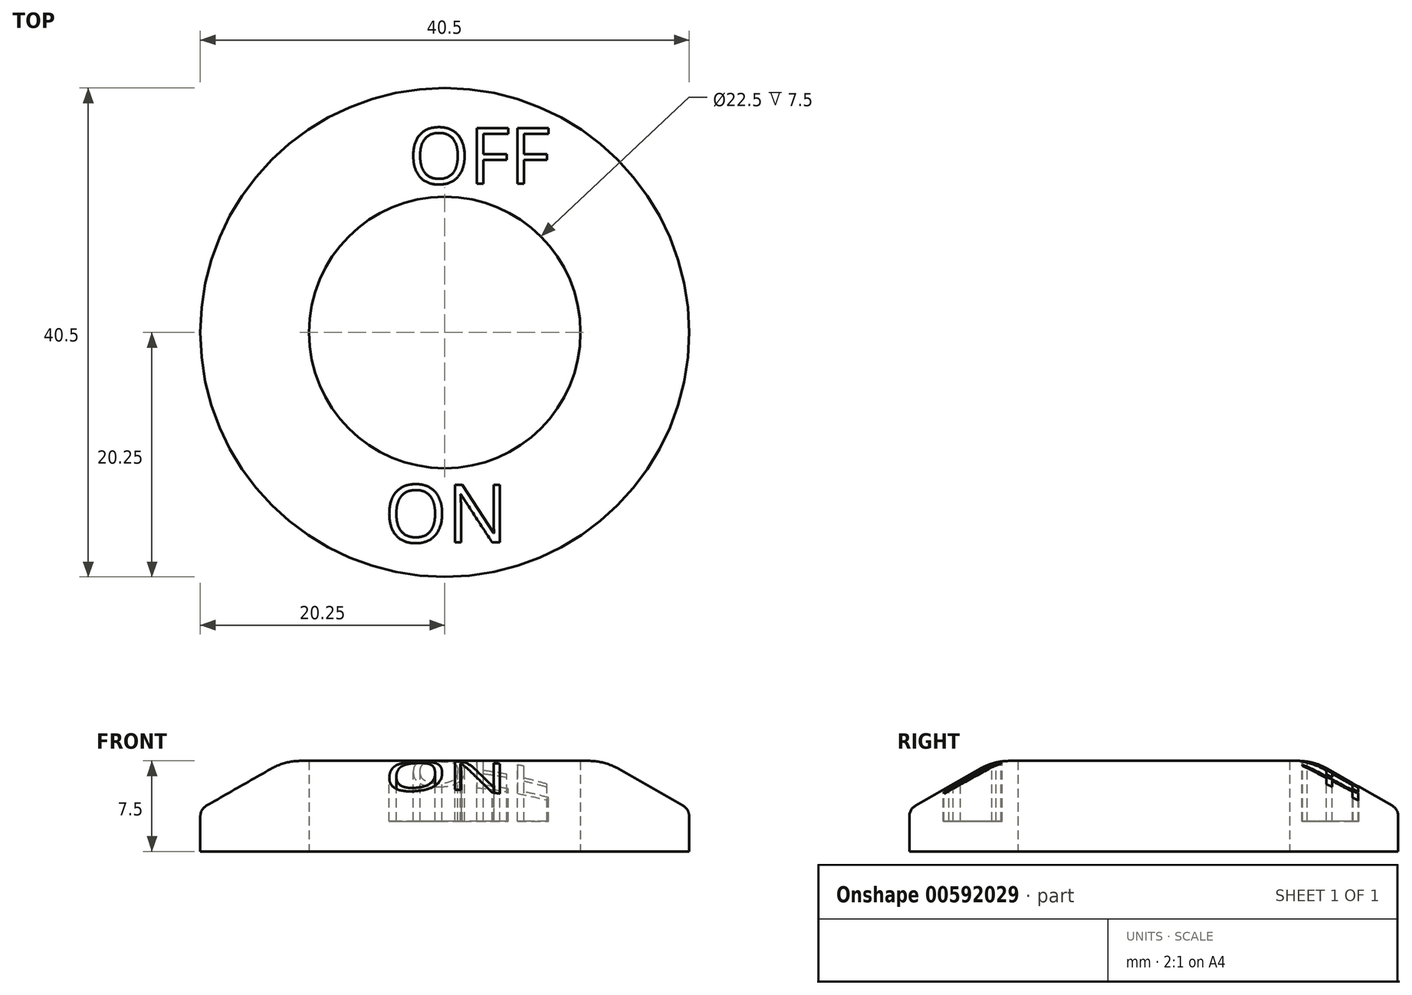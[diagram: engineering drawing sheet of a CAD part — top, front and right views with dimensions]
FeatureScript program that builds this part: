
annotation { "Feature Type Name" : "Feature", "Feature Type Description" : "" }
export const myFeature = defineFeature(function(context is Context, id is Id, definition is map)
    precondition{}
    {
        {
            var Q0;
            Q0=qCreatedBy(makeId("Top.planeOp"),FACE);
            var sketch = newSketch(context, id + "F0", { "sketchPlane" : qUnion([Q0])});
            skCircle(sketch, "E0", {"center": v(0, 0) * mm, "radius": 20.25 * mm});
            skSolve(sketch);
        }
        {
            var Q0;
            Q0=qCreatedBy(makeId("Top.planeOp"),FACE);
            cPlane(context, id + "F1", {"entities" : qUnion([Q0]), "cplaneType" : CPlaneType.OFFSET, "offset" : 7.5 * mm, "width" : 150 * mm, "height" : 150 * mm});
        }
        {
            var Q0;
            Q0=qCreatedBy(id+"F1.planeOp",FACE);
            var sketch = newSketch(context, id + "F2", { "sketchPlane" : qUnion([Q0])});
            skCircle(sketch, "E1", {"center": v(0, 0) * mm, "radius": 13.25 * mm});
            skSolve(sketch);
        }
        {
            var Q0;
            Q0=makeQuery(id+"F0.imprint","IMPRINT",FACE,{"disambiguationData":[TD([[makeQuery(id+"F0.imprint","IMPRINT",EDGE,{"derivedFrom":sQuery(id+"F0.wireOp",EDGE,"E0")}),1.0]])]});
            extrude(context, id + "F3", {"entities" : qUnion([Q0]), "depth" : 3.5 * mm, "offsetDistance" : 25 * mm});
        }
        {
            var Q0;
            Q0=makeQuery(id+"F3.opExtrude","CAP_FACE",FACE,{"disambiguationData":[OSD([sQuery(id+"F0.wireOp",EDGE,"E0")])],"isStart":false});
            var Q1;
            Q1=makeQuery(id+"F2.imprint","IMPRINT",FACE,{"disambiguationData":[TD([[makeQuery(id+"F2.imprint","IMPRINT",EDGE,{"derivedFrom":sQuery(id+"F2.wireOp",EDGE,"E1")}),1.0]])]});
            loft(context, id + "F4", {"operationType" : NewBodyOperationType.ADD, "sheetProfilesArray" : [{ "sheetProfileEntities" : qUnion([Q0]) }, { "sheetProfileEntities" : qUnion([Q1]) }]});
        }
        {
            var Q0;
            Q0=sQuery(id+"F0.wireOp",VERTEX,"E0.center");
            var Q1;
            Q1=makeQuery(id+"F3.opExtrude","SWEPT_BODY",BODY,{"disambiguationData":[OSD([sQuery(id+"F0.wireOp",EDGE,"E0")])]});
            hole(context, id + "F5", {"style" : HoleStyle.SIMPLE, "endStyle" : HoleEndStyle.BLIND, "oppositeDirection" : true, "holeDiameter" : 22.5 * mm, "majorDiameter" : 5 * mm, "holeDepth" : 30 * mm, "isTappedThrough" : true, "tappedDepth" : 12 * mm, "tapClearance" : 3, "locations" : qUnion([Q0]), "scope" : qUnion([Q1])});
        }
        {
            var Q0;
            Q0=makeQuery(id+"F4.opLoft","MID_CAP_EDGE",EDGE,{"disambiguationData":[OSD([sQuery(id+"F2.wireOp",EDGE,"E1")])],"capPos":1.0});
            fillet(context, id + "F6", {"entities" : qUnion([Q0]), "tangentPropagation" : true, "radius" : 5 * mm, "defaultsChanged" : false, "vertexSettings" : [], "allowEdgeOverflow" : false});
        }
        {
            var Q0;
            {var subQ0=sQuery(id+"F0.wireOp",EDGE,"E0");Q0=makeQuery(id+"F4.boolean.opBoolean","MERGE",EDGE,{"derivedFrom":[makeQuery(id+"F3.opExtrude","CAP_EDGE",EDGE,{"disambiguationData":[OSD([subQ0])],"isStart":false}),makeQuery(id+"F4.opLoft","MID_CAP_EDGE",EDGE,{"disambiguationData":[OSD([subQ0])],"capPos":0.0})]});}
            fillet(context, id + "F7", {"entities" : qUnion([Q0]), "tangentPropagation" : true, "radius" : 1 * mm, "defaultsChanged" : false, "vertexSettings" : [], "allowEdgeOverflow" : false});
        }
        {
            var Q0;
            Q0=qCreatedBy(id+"F1.planeOp",FACE);
            var sketch = newSketch(context, id + "F8", { "sketchPlane" : qUnion([Q0])});
            skText(sketch, "E2", { "text": "ON", "fontName": "OpenSans-Regular.ttf"});
            skText(sketch, "E3", { "text": "OFF\n", "fontName": "OpenSans-Regular.ttf"});
            const initialGuessF8  = {"E2": [-0.005, -0.0174, 1, 0, 0.0048], "E3": [-0.003, 0.01232, 1, 0, 0.00466]};
            skSetInitialGuess(sketch, initialGuessF8);
            skSolve(sketch);
        }
        {
            var Q0;
            Q0 = qSketchRegion(id + "F8", true);
            extrude(context, id + "F9", {"entities" : qUnion([Q0]), "operationType" : NewBodyOperationType.REMOVE, "oppositeDirection" : true, "depth" : 5 * mm, "offsetDistance" : 25 * mm});
        }
    });
